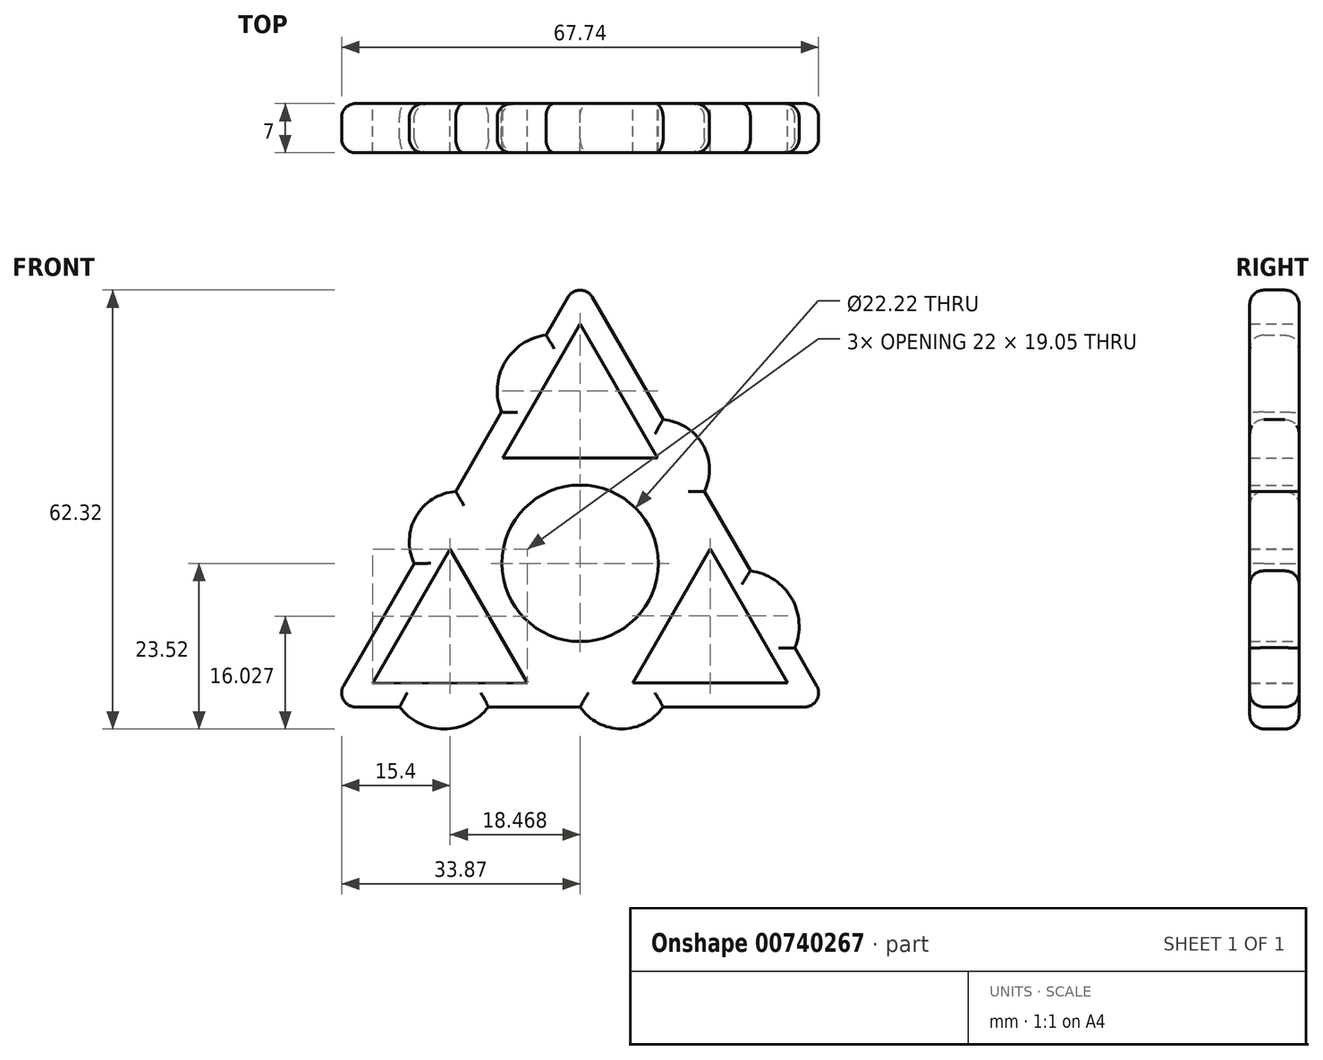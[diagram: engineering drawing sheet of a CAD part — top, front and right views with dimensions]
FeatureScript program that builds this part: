
annotation { "Feature Type Name" : "Feature", "Feature Type Description" : "" }
export const myFeature = defineFeature(function(context is Context, id is Id, definition is map)
    precondition{}
    {
        {
            var Q0;
            Q0=qCreatedBy(makeId("Front.planeOp"),FACE);
            var sketch = newSketch(context, id + "F0", { "sketchPlane" : qUnion([Q0])});
            skCircle(sketch, "E0", {"center": v(0, 0) * mm, "radius": 11.1 * mm});
            skLineSegment(sketch, "E1.0", {"start": v(-35.34, -20.4) * mm, "end": v(0, 40.8) * mm});
            skLineSegment(sketch, "E1.1", {"start": v(0, 40.8) * mm, "end": v(35.34, -20.4) * mm});
            skLineSegment(sketch, "E1.2", {"start": v(35.34, -20.4) * mm, "end": v(-35.33, -20.4) * mm});
            skLineSegment(sketch, "E2.direction1", {"start": v(0, 0.8) * mm, "end": v(25, 0.8) * mm, "construction": true});
            skLineSegment(sketch, "E3.0", {"start": v(-11, 14.98) * mm, "end": v(0, 34.03) * mm});
            skLineSegment(sketch, "E3.1", {"start": v(-11, 14.98) * mm, "end": v(11, 14.98) * mm});
            skLineSegment(sketch, "E3.2", {"start": v(0, 34.03) * mm, "end": v(11, 14.98) * mm});
            skLineSegment(sketch, "E4.0", {"start": v(-18.58, -76.36) * mm, "end": v(-40.67, -38.1) * mm});
            skLineSegment(sketch, "E4.1", {"start": v(-18.58, -76.36) * mm, "end": v(3.5, -38.1) * mm});
            skLineSegment(sketch, "E5.1.0", {"start": v(-7.47, -17.02) * mm, "end": v(-18.47, 2.03) * mm});
            skLineSegment(sketch, "E5.1.1", {"start": v(-7.47, -17.02) * mm, "end": v(-29.47, -17.02) * mm});
            skLineSegment(sketch, "E5.1.2", {"start": v(-29.47, -17.02) * mm, "end": v(-18.47, 2.03) * mm});
            skLineSegment(sketch, "E5.2.0", {"start": v(18.47, 2.04) * mm, "end": v(7.48, -17.01) * mm});
            skLineSegment(sketch, "E5.2.1", {"start": v(18.47, 2.04) * mm, "end": v(29.47, -17.01) * mm});
            skLineSegment(sketch, "E5.2.2", {"start": v(29.47, -17.01) * mm, "end": v(7.48, -17.01) * mm});
            skArc(sketch, "E6", {"start": v(-4.85, 32.4) * mm, "mid": v(-10.71, 28.5) * mm, "end": v(-11.16, 21.48) * mm});
            skArc(sketch, "E7", {"start": v(-17.67, 10.2) * mm, "mid": v(-23.3, 6.66) * mm, "end": v(-23.56, 0) * mm});
            skArc(sketch, "E8.1.0", {"start": v(-25.63, -20.4) * mm, "mid": v(-19.32, -23.52) * mm, "end": v(-13.02, -20.4) * mm});
            skArc(sketch, "E8.1.1", {"start": v(0, -20.4) * mm, "mid": v(5.89, -23.51) * mm, "end": v(11.78, -20.4) * mm});
            skArc(sketch, "E8.2.0", {"start": v(30.48, -12) * mm, "mid": v(30.04, -4.97) * mm, "end": v(24.18, -1.08) * mm});
            skArc(sketch, "E8.2.1", {"start": v(17.67, 10.2) * mm, "mid": v(17.42, 16.86) * mm, "end": v(11.78, 20.4) * mm});
            skSolve(sketch);
        }
        {
            var Q0;
            Q0 = qSketchRegion(id + "F0", true);
            extrude(context, id + "F1", {"entities" : qUnion([Q0]), "depth" : 7 * mm, "offsetDistance" : 25 * mm});
        }
        {
            var Q0;
            Q0=makeQuery(id+"F1.opExtrude","SWEPT_EDGE",EDGE,{"disambiguationData":[OSD([sQuery(id+"F0.wireOp",EDGE,"E1.0"),sQuery(id+"F0.wireOp",EDGE,"E1.1"),sQuery(id+"F0.wireOp",EDGE,"TbrVNuta-voQp-v51U-YrGK-JMvI6IDHDoPP")])]});
            var Q1;
            Q1=makeQuery(id+"F1.opExtrude","SWEPT_EDGE",EDGE,{"disambiguationData":[OSD([sQuery(id+"F0.wireOp",EDGE,"E1.0"),sQuery(id+"F0.wireOp",EDGE,"E1.2")])]});
            var Q2;
            Q2=makeQuery(id+"F1.opExtrude","SWEPT_EDGE",EDGE,{"disambiguationData":[OSD([sQuery(id+"F0.wireOp",EDGE,"E1.1"),sQuery(id+"F0.wireOp",EDGE,"E1.2")])]});
            fillet(context, id + "F2", {"entities" : qUnion([Q0, Q1, Q2]), "radius" : 2 * mm, "tangentPropagation" : true, "allowEdgeOverflow" : false});
        }
        {
            var Q0;
            {var subQ0=sQuery(id+"F0.wireOp",EDGE,"E1.0");Q0=makeQuery(id+"F1.opExtrude","CAP_EDGE",EDGE,{"disambiguationData":[OSD([subQ0]),TDD([makeQuery(id+"F0.imprint","IMPRINT",EDGE,{"disambiguationData":[TD([[makeQuery(id+"F0.imprint","INTERSECT",VERTEX,{"derivedFrom":[subQ0,sQuery(id+"F0.wireOp",EDGE,"E1.2")]}),-1.0]])],"derivedFrom":subQ0})])],"isStart":false});}
            var Q1;
            Q1=makeQuery(id+"F1.opExtrude","CAP_EDGE",EDGE,{"disambiguationData":[OSD([sQuery(id+"F0.wireOp",EDGE,"E7")])],"isStart":false});
            var Q2;
            {var subQ0=sQuery(id+"F0.wireOp",EDGE,"E1.0");Q2=makeQuery(id+"F1.opExtrude","CAP_EDGE",EDGE,{"disambiguationData":[OSD([subQ0]),TDD([makeQuery(id+"F0.imprint","IMPRINT",EDGE,{"disambiguationData":[TD([[makeQuery(id+"F0.imprint","INTERSECT",VERTEX,{"disambiguationData":[OD(1.0)],"derivedFrom":[subQ0,sQuery(id+"F0.wireOp",EDGE,"E6")]}),1.0]])],"derivedFrom":subQ0})])],"isStart":false});}
            var Q3;
            Q3=makeQuery(id+"F1.opExtrude","CAP_EDGE",EDGE,{"disambiguationData":[OSD([sQuery(id+"F0.wireOp",EDGE,"E6")])],"isStart":false});
            var Q4;
            {var subQ0=sQuery(id+"F0.wireOp",EDGE,"E1.0");Q4=makeQuery(id+"F1.opExtrude","CAP_EDGE",EDGE,{"disambiguationData":[OSD([subQ0]),TDD([makeQuery(id+"F0.imprint","IMPRINT",EDGE,{"disambiguationData":[TD([[makeQuery(id+"F0.imprint","INTERSECT",VERTEX,{"derivedFrom":[subQ0,sQuery(id+"F0.wireOp",EDGE,"E1.1")]}),1.0]])],"derivedFrom":subQ0})])],"isStart":false});}
            var Q5;
            {var subQ0=sQuery(id+"F0.wireOp",EDGE,"E1.1");var subQ1=sQuery(id+"F0.wireOp",EDGE,"E1.0");Q5=makeQuery(id+"F2.opFillet","BLEND_EDGE",EDGE,{"blendedFrom":[makeQuery(id+"F1.opExtrude","SWEPT_EDGE",EDGE,{"disambiguationData":[OSD([subQ1,subQ0])]}),makeQuery(id+"F1.opExtrude","CAP_FACE",FACE,{"disambiguationData":[OSD([sQuery(id+"F0.wireOp",EDGE,"E0"),subQ1,subQ0,sQuery(id+"F0.wireOp",EDGE,"E1.2"),sQuery(id+"F0.wireOp",EDGE,"E3.0"),sQuery(id+"F0.wireOp",EDGE,"E3.1"),sQuery(id+"F0.wireOp",EDGE,"E3.2"),sQuery(id+"F0.wireOp",EDGE,"E5.1.0"),sQuery(id+"F0.wireOp",EDGE,"E5.1.1"),sQuery(id+"F0.wireOp",EDGE,"E5.1.2"),sQuery(id+"F0.wireOp",EDGE,"E5.2.0"),sQuery(id+"F0.wireOp",EDGE,"E5.2.1"),sQuery(id+"F0.wireOp",EDGE,"E5.2.2"),sQuery(id+"F0.wireOp",EDGE,"E6"),sQuery(id+"F0.wireOp",EDGE,"E7"),sQuery(id+"F0.wireOp",EDGE,"E8.1.0"),sQuery(id+"F0.wireOp",EDGE,"E8.1.1"),sQuery(id+"F0.wireOp",EDGE,"E8.2.0"),sQuery(id+"F0.wireOp",EDGE,"E8.2.1")])],"isStart":false})],"blendedInto":[makeQuery(id+"F1.opExtrude","CAP_FACE",FACE,{"disambiguationData":[OSD([sQuery(id+"F0.wireOp",EDGE,"E0"),subQ1,subQ0,sQuery(id+"F0.wireOp",EDGE,"E1.2"),sQuery(id+"F0.wireOp",EDGE,"E3.0"),sQuery(id+"F0.wireOp",EDGE,"E3.1"),sQuery(id+"F0.wireOp",EDGE,"E3.2"),sQuery(id+"F0.wireOp",EDGE,"E5.1.0"),sQuery(id+"F0.wireOp",EDGE,"E5.1.1"),sQuery(id+"F0.wireOp",EDGE,"E5.1.2"),sQuery(id+"F0.wireOp",EDGE,"E5.2.0"),sQuery(id+"F0.wireOp",EDGE,"E5.2.1"),sQuery(id+"F0.wireOp",EDGE,"E5.2.2"),sQuery(id+"F0.wireOp",EDGE,"E6"),sQuery(id+"F0.wireOp",EDGE,"E7"),sQuery(id+"F0.wireOp",EDGE,"E8.1.0"),sQuery(id+"F0.wireOp",EDGE,"E8.1.1"),sQuery(id+"F0.wireOp",EDGE,"E8.2.0"),sQuery(id+"F0.wireOp",EDGE,"E8.2.1")])],"isStart":false})]});}
            var Q6;
            {var subQ0=sQuery(id+"F0.wireOp",EDGE,"E1.1");Q6=makeQuery(id+"F1.opExtrude","CAP_EDGE",EDGE,{"disambiguationData":[OSD([subQ0]),TDD([makeQuery(id+"F0.imprint","IMPRINT",EDGE,{"disambiguationData":[TD([[makeQuery(id+"F0.imprint","INTERSECT",VERTEX,{"derivedFrom":[sQuery(id+"F0.wireOp",EDGE,"E1.0"),subQ0]}),-1.0]])],"derivedFrom":subQ0})])],"isStart":false});}
            var Q7;
            Q7=makeQuery(id+"F1.opExtrude","CAP_EDGE",EDGE,{"disambiguationData":[OSD([sQuery(id+"F0.wireOp",EDGE,"E8.2.1")])],"isStart":false});
            var Q8;
            {var subQ0=sQuery(id+"F0.wireOp",EDGE,"E1.1");Q8=makeQuery(id+"F1.opExtrude","CAP_EDGE",EDGE,{"disambiguationData":[OSD([subQ0]),TDD([makeQuery(id+"F0.imprint","IMPRINT",EDGE,{"disambiguationData":[TD([[makeQuery(id+"F0.imprint","INTERSECT",VERTEX,{"disambiguationData":[OD(1.0)],"derivedFrom":[subQ0,sQuery(id+"F0.wireOp",EDGE,"E8.2.0")]}),1.0]])],"derivedFrom":subQ0})])],"isStart":false});}
            var Q9;
            Q9=makeQuery(id+"F1.opExtrude","CAP_EDGE",EDGE,{"disambiguationData":[OSD([sQuery(id+"F0.wireOp",EDGE,"E8.2.0")])],"isStart":false});
            var Q10;
            {var subQ0=sQuery(id+"F0.wireOp",EDGE,"E1.1");Q10=makeQuery(id+"F1.opExtrude","CAP_EDGE",EDGE,{"disambiguationData":[OSD([subQ0]),TDD([makeQuery(id+"F0.imprint","IMPRINT",EDGE,{"disambiguationData":[TD([[makeQuery(id+"F0.imprint","INTERSECT",VERTEX,{"derivedFrom":[subQ0,sQuery(id+"F0.wireOp",EDGE,"E1.2")]}),1.0]])],"derivedFrom":subQ0})])],"isStart":false});}
            var Q11;
            {var subQ0=sQuery(id+"F0.wireOp",EDGE,"E1.2");Q11=makeQuery(id+"F1.opExtrude","CAP_EDGE",EDGE,{"disambiguationData":[OSD([subQ0]),TDD([makeQuery(id+"F0.imprint","IMPRINT",EDGE,{"disambiguationData":[TD([[makeQuery(id+"F0.imprint","INTERSECT",VERTEX,{"derivedFrom":[sQuery(id+"F0.wireOp",EDGE,"E1.1"),subQ0]}),-1.0]])],"derivedFrom":subQ0})])],"isStart":false});}
            var Q12;
            {var subQ0=sQuery(id+"F0.wireOp",EDGE,"E1.2");var subQ1=sQuery(id+"F0.wireOp",EDGE,"E1.1");Q12=makeQuery(id+"F2.opFillet","BLEND_EDGE",EDGE,{"blendedFrom":[makeQuery(id+"F1.opExtrude","SWEPT_EDGE",EDGE,{"disambiguationData":[OSD([subQ1,subQ0])]}),makeQuery(id+"F1.opExtrude","CAP_FACE",FACE,{"disambiguationData":[OSD([sQuery(id+"F0.wireOp",EDGE,"E0"),sQuery(id+"F0.wireOp",EDGE,"E1.0"),subQ1,subQ0,sQuery(id+"F0.wireOp",EDGE,"E3.0"),sQuery(id+"F0.wireOp",EDGE,"E3.1"),sQuery(id+"F0.wireOp",EDGE,"E3.2"),sQuery(id+"F0.wireOp",EDGE,"E5.1.0"),sQuery(id+"F0.wireOp",EDGE,"E5.1.1"),sQuery(id+"F0.wireOp",EDGE,"E5.1.2"),sQuery(id+"F0.wireOp",EDGE,"E5.2.0"),sQuery(id+"F0.wireOp",EDGE,"E5.2.1"),sQuery(id+"F0.wireOp",EDGE,"E5.2.2"),sQuery(id+"F0.wireOp",EDGE,"E6"),sQuery(id+"F0.wireOp",EDGE,"E7"),sQuery(id+"F0.wireOp",EDGE,"E8.1.0"),sQuery(id+"F0.wireOp",EDGE,"E8.1.1"),sQuery(id+"F0.wireOp",EDGE,"E8.2.0"),sQuery(id+"F0.wireOp",EDGE,"E8.2.1")])],"isStart":false})],"blendedInto":[makeQuery(id+"F1.opExtrude","CAP_FACE",FACE,{"disambiguationData":[OSD([sQuery(id+"F0.wireOp",EDGE,"E0"),sQuery(id+"F0.wireOp",EDGE,"E1.0"),subQ1,subQ0,sQuery(id+"F0.wireOp",EDGE,"E3.0"),sQuery(id+"F0.wireOp",EDGE,"E3.1"),sQuery(id+"F0.wireOp",EDGE,"E3.2"),sQuery(id+"F0.wireOp",EDGE,"E5.1.0"),sQuery(id+"F0.wireOp",EDGE,"E5.1.1"),sQuery(id+"F0.wireOp",EDGE,"E5.1.2"),sQuery(id+"F0.wireOp",EDGE,"E5.2.0"),sQuery(id+"F0.wireOp",EDGE,"E5.2.1"),sQuery(id+"F0.wireOp",EDGE,"E5.2.2"),sQuery(id+"F0.wireOp",EDGE,"E6"),sQuery(id+"F0.wireOp",EDGE,"E7"),sQuery(id+"F0.wireOp",EDGE,"E8.1.0"),sQuery(id+"F0.wireOp",EDGE,"E8.1.1"),sQuery(id+"F0.wireOp",EDGE,"E8.2.0"),sQuery(id+"F0.wireOp",EDGE,"E8.2.1")])],"isStart":false})]});}
            var Q13;
            Q13=makeQuery(id+"F1.opExtrude","CAP_EDGE",EDGE,{"disambiguationData":[OSD([sQuery(id+"F0.wireOp",EDGE,"E8.1.1")])],"isStart":false});
            var Q14;
            {var subQ0=sQuery(id+"F0.wireOp",EDGE,"E1.2");Q14=makeQuery(id+"F1.opExtrude","CAP_EDGE",EDGE,{"disambiguationData":[OSD([subQ0]),TDD([makeQuery(id+"F0.imprint","IMPRINT",EDGE,{"disambiguationData":[TD([[makeQuery(id+"F0.imprint","INTERSECT",VERTEX,{"disambiguationData":[OD(1.0)],"derivedFrom":[subQ0,sQuery(id+"F0.wireOp",EDGE,"E8.1.0")]}),1.0]])],"derivedFrom":subQ0})])],"isStart":false});}
            var Q15;
            Q15=makeQuery(id+"F1.opExtrude","CAP_EDGE",EDGE,{"disambiguationData":[OSD([sQuery(id+"F0.wireOp",EDGE,"E8.1.0")])],"isStart":false});
            var Q16;
            {var subQ0=sQuery(id+"F0.wireOp",EDGE,"E1.2");Q16=makeQuery(id+"F1.opExtrude","CAP_EDGE",EDGE,{"disambiguationData":[OSD([subQ0]),TDD([makeQuery(id+"F0.imprint","IMPRINT",EDGE,{"disambiguationData":[TD([[makeQuery(id+"F0.imprint","INTERSECT",VERTEX,{"derivedFrom":[sQuery(id+"F0.wireOp",EDGE,"E1.0"),subQ0]}),1.0]])],"derivedFrom":subQ0})])],"isStart":false});}
            var Q17;
            {var subQ0=sQuery(id+"F0.wireOp",EDGE,"E1.2");var subQ1=sQuery(id+"F0.wireOp",EDGE,"E1.0");Q17=makeQuery(id+"F2.opFillet","BLEND_EDGE",EDGE,{"blendedFrom":[makeQuery(id+"F1.opExtrude","SWEPT_EDGE",EDGE,{"disambiguationData":[OSD([subQ1,subQ0])]}),makeQuery(id+"F1.opExtrude","CAP_FACE",FACE,{"disambiguationData":[OSD([sQuery(id+"F0.wireOp",EDGE,"E0"),subQ1,sQuery(id+"F0.wireOp",EDGE,"E1.1"),subQ0,sQuery(id+"F0.wireOp",EDGE,"E3.0"),sQuery(id+"F0.wireOp",EDGE,"E3.1"),sQuery(id+"F0.wireOp",EDGE,"E3.2"),sQuery(id+"F0.wireOp",EDGE,"E5.1.0"),sQuery(id+"F0.wireOp",EDGE,"E5.1.1"),sQuery(id+"F0.wireOp",EDGE,"E5.1.2"),sQuery(id+"F0.wireOp",EDGE,"E5.2.0"),sQuery(id+"F0.wireOp",EDGE,"E5.2.1"),sQuery(id+"F0.wireOp",EDGE,"E5.2.2"),sQuery(id+"F0.wireOp",EDGE,"E6"),sQuery(id+"F0.wireOp",EDGE,"E7"),sQuery(id+"F0.wireOp",EDGE,"E8.1.0"),sQuery(id+"F0.wireOp",EDGE,"E8.1.1"),sQuery(id+"F0.wireOp",EDGE,"E8.2.0"),sQuery(id+"F0.wireOp",EDGE,"E8.2.1")])],"isStart":false})],"blendedInto":[makeQuery(id+"F1.opExtrude","CAP_FACE",FACE,{"disambiguationData":[OSD([sQuery(id+"F0.wireOp",EDGE,"E0"),subQ1,sQuery(id+"F0.wireOp",EDGE,"E1.1"),subQ0,sQuery(id+"F0.wireOp",EDGE,"E3.0"),sQuery(id+"F0.wireOp",EDGE,"E3.1"),sQuery(id+"F0.wireOp",EDGE,"E3.2"),sQuery(id+"F0.wireOp",EDGE,"E5.1.0"),sQuery(id+"F0.wireOp",EDGE,"E5.1.1"),sQuery(id+"F0.wireOp",EDGE,"E5.1.2"),sQuery(id+"F0.wireOp",EDGE,"E5.2.0"),sQuery(id+"F0.wireOp",EDGE,"E5.2.1"),sQuery(id+"F0.wireOp",EDGE,"E5.2.2"),sQuery(id+"F0.wireOp",EDGE,"E6"),sQuery(id+"F0.wireOp",EDGE,"E7"),sQuery(id+"F0.wireOp",EDGE,"E8.1.0"),sQuery(id+"F0.wireOp",EDGE,"E8.1.1"),sQuery(id+"F0.wireOp",EDGE,"E8.2.0"),sQuery(id+"F0.wireOp",EDGE,"E8.2.1")])],"isStart":false})]});}
            fillet(context, id + "F3", {"entities" : qUnion([Q0, Q1, Q2, Q3, Q4, Q5, Q6, Q7, Q8, Q9, Q10, Q11, Q12, Q13, Q14, Q15, Q16, Q17]), "radius" : 2 * mm, "tangentPropagation" : true, "allowEdgeOverflow" : false});
        }
        {
            var Q0;
            {var subQ0=sQuery(id+"F0.wireOp",EDGE,"E1.1");var subQ1=sQuery(id+"F0.wireOp",EDGE,"E1.0");Q0=makeQuery(id+"F2.opFillet","BLEND_EDGE",EDGE,{"blendedFrom":[makeQuery(id+"F1.opExtrude","SWEPT_EDGE",EDGE,{"disambiguationData":[OSD([subQ1,subQ0])]}),makeQuery(id+"F1.opExtrude","CAP_FACE",FACE,{"disambiguationData":[OSD([sQuery(id+"F0.wireOp",EDGE,"E0"),subQ1,subQ0,sQuery(id+"F0.wireOp",EDGE,"E1.2"),sQuery(id+"F0.wireOp",EDGE,"E3.0"),sQuery(id+"F0.wireOp",EDGE,"E3.1"),sQuery(id+"F0.wireOp",EDGE,"E3.2"),sQuery(id+"F0.wireOp",EDGE,"E5.1.0"),sQuery(id+"F0.wireOp",EDGE,"E5.1.1"),sQuery(id+"F0.wireOp",EDGE,"E5.1.2"),sQuery(id+"F0.wireOp",EDGE,"E5.2.0"),sQuery(id+"F0.wireOp",EDGE,"E5.2.1"),sQuery(id+"F0.wireOp",EDGE,"E5.2.2"),sQuery(id+"F0.wireOp",EDGE,"E6"),sQuery(id+"F0.wireOp",EDGE,"E7"),sQuery(id+"F0.wireOp",EDGE,"E8.1.0"),sQuery(id+"F0.wireOp",EDGE,"E8.1.1"),sQuery(id+"F0.wireOp",EDGE,"E8.2.0"),sQuery(id+"F0.wireOp",EDGE,"E8.2.1")])],"isStart":true})],"blendedInto":[makeQuery(id+"F1.opExtrude","CAP_FACE",FACE,{"disambiguationData":[OSD([sQuery(id+"F0.wireOp",EDGE,"E0"),subQ1,subQ0,sQuery(id+"F0.wireOp",EDGE,"E1.2"),sQuery(id+"F0.wireOp",EDGE,"E3.0"),sQuery(id+"F0.wireOp",EDGE,"E3.1"),sQuery(id+"F0.wireOp",EDGE,"E3.2"),sQuery(id+"F0.wireOp",EDGE,"E5.1.0"),sQuery(id+"F0.wireOp",EDGE,"E5.1.1"),sQuery(id+"F0.wireOp",EDGE,"E5.1.2"),sQuery(id+"F0.wireOp",EDGE,"E5.2.0"),sQuery(id+"F0.wireOp",EDGE,"E5.2.1"),sQuery(id+"F0.wireOp",EDGE,"E5.2.2"),sQuery(id+"F0.wireOp",EDGE,"E6"),sQuery(id+"F0.wireOp",EDGE,"E7"),sQuery(id+"F0.wireOp",EDGE,"E8.1.0"),sQuery(id+"F0.wireOp",EDGE,"E8.1.1"),sQuery(id+"F0.wireOp",EDGE,"E8.2.0"),sQuery(id+"F0.wireOp",EDGE,"E8.2.1")])],"isStart":true})]});}
            var Q1;
            {var subQ0=sQuery(id+"F0.wireOp",EDGE,"E1.1");Q1=makeQuery(id+"F1.opExtrude","CAP_EDGE",EDGE,{"disambiguationData":[OSD([subQ0]),TDD([makeQuery(id+"F0.imprint","IMPRINT",EDGE,{"disambiguationData":[TD([[makeQuery(id+"F0.imprint","INTERSECT",VERTEX,{"derivedFrom":[sQuery(id+"F0.wireOp",EDGE,"E1.0"),subQ0]}),-1.0]])],"derivedFrom":subQ0})])],"isStart":true});}
            var Q2;
            {var subQ0=sQuery(id+"F0.wireOp",EDGE,"E1.0");Q2=makeQuery(id+"F1.opExtrude","CAP_EDGE",EDGE,{"disambiguationData":[OSD([subQ0]),TDD([makeQuery(id+"F0.imprint","IMPRINT",EDGE,{"disambiguationData":[TD([[makeQuery(id+"F0.imprint","INTERSECT",VERTEX,{"derivedFrom":[subQ0,sQuery(id+"F0.wireOp",EDGE,"E1.1")]}),1.0]])],"derivedFrom":subQ0})])],"isStart":true});}
            var Q3;
            Q3=makeQuery(id+"F1.opExtrude","CAP_EDGE",EDGE,{"disambiguationData":[OSD([sQuery(id+"F0.wireOp",EDGE,"E6")])],"isStart":true});
            var Q4;
            {var subQ0=sQuery(id+"F0.wireOp",EDGE,"E1.0");Q4=makeQuery(id+"F1.opExtrude","CAP_EDGE",EDGE,{"disambiguationData":[OSD([subQ0]),TDD([makeQuery(id+"F0.imprint","IMPRINT",EDGE,{"disambiguationData":[TD([[makeQuery(id+"F0.imprint","INTERSECT",VERTEX,{"disambiguationData":[OD(1.0)],"derivedFrom":[subQ0,sQuery(id+"F0.wireOp",EDGE,"E6")]}),1.0]])],"derivedFrom":subQ0})])],"isStart":true});}
            var Q5;
            Q5=makeQuery(id+"F1.opExtrude","CAP_EDGE",EDGE,{"disambiguationData":[OSD([sQuery(id+"F0.wireOp",EDGE,"E7")])],"isStart":true});
            var Q6;
            {var subQ0=sQuery(id+"F0.wireOp",EDGE,"E1.0");Q6=makeQuery(id+"F1.opExtrude","CAP_EDGE",EDGE,{"disambiguationData":[OSD([subQ0]),TDD([makeQuery(id+"F0.imprint","IMPRINT",EDGE,{"disambiguationData":[TD([[makeQuery(id+"F0.imprint","INTERSECT",VERTEX,{"derivedFrom":[subQ0,sQuery(id+"F0.wireOp",EDGE,"E1.2")]}),-1.0]])],"derivedFrom":subQ0})])],"isStart":true});}
            var Q7;
            {var subQ0=sQuery(id+"F0.wireOp",EDGE,"E1.2");var subQ1=sQuery(id+"F0.wireOp",EDGE,"E1.0");Q7=makeQuery(id+"F2.opFillet","BLEND_EDGE",EDGE,{"blendedFrom":[makeQuery(id+"F1.opExtrude","SWEPT_EDGE",EDGE,{"disambiguationData":[OSD([subQ1,subQ0])]}),makeQuery(id+"F1.opExtrude","CAP_FACE",FACE,{"disambiguationData":[OSD([sQuery(id+"F0.wireOp",EDGE,"E0"),subQ1,sQuery(id+"F0.wireOp",EDGE,"E1.1"),subQ0,sQuery(id+"F0.wireOp",EDGE,"E3.0"),sQuery(id+"F0.wireOp",EDGE,"E3.1"),sQuery(id+"F0.wireOp",EDGE,"E3.2"),sQuery(id+"F0.wireOp",EDGE,"E5.1.0"),sQuery(id+"F0.wireOp",EDGE,"E5.1.1"),sQuery(id+"F0.wireOp",EDGE,"E5.1.2"),sQuery(id+"F0.wireOp",EDGE,"E5.2.0"),sQuery(id+"F0.wireOp",EDGE,"E5.2.1"),sQuery(id+"F0.wireOp",EDGE,"E5.2.2"),sQuery(id+"F0.wireOp",EDGE,"E6"),sQuery(id+"F0.wireOp",EDGE,"E7"),sQuery(id+"F0.wireOp",EDGE,"E8.1.0"),sQuery(id+"F0.wireOp",EDGE,"E8.1.1"),sQuery(id+"F0.wireOp",EDGE,"E8.2.0"),sQuery(id+"F0.wireOp",EDGE,"E8.2.1")])],"isStart":true})],"blendedInto":[makeQuery(id+"F1.opExtrude","CAP_FACE",FACE,{"disambiguationData":[OSD([sQuery(id+"F0.wireOp",EDGE,"E0"),subQ1,sQuery(id+"F0.wireOp",EDGE,"E1.1"),subQ0,sQuery(id+"F0.wireOp",EDGE,"E3.0"),sQuery(id+"F0.wireOp",EDGE,"E3.1"),sQuery(id+"F0.wireOp",EDGE,"E3.2"),sQuery(id+"F0.wireOp",EDGE,"E5.1.0"),sQuery(id+"F0.wireOp",EDGE,"E5.1.1"),sQuery(id+"F0.wireOp",EDGE,"E5.1.2"),sQuery(id+"F0.wireOp",EDGE,"E5.2.0"),sQuery(id+"F0.wireOp",EDGE,"E5.2.1"),sQuery(id+"F0.wireOp",EDGE,"E5.2.2"),sQuery(id+"F0.wireOp",EDGE,"E6"),sQuery(id+"F0.wireOp",EDGE,"E7"),sQuery(id+"F0.wireOp",EDGE,"E8.1.0"),sQuery(id+"F0.wireOp",EDGE,"E8.1.1"),sQuery(id+"F0.wireOp",EDGE,"E8.2.0"),sQuery(id+"F0.wireOp",EDGE,"E8.2.1")])],"isStart":true})]});}
            var Q8;
            {var subQ0=sQuery(id+"F0.wireOp",EDGE,"E1.2");Q8=makeQuery(id+"F1.opExtrude","CAP_EDGE",EDGE,{"disambiguationData":[OSD([subQ0]),TDD([makeQuery(id+"F0.imprint","IMPRINT",EDGE,{"disambiguationData":[TD([[makeQuery(id+"F0.imprint","INTERSECT",VERTEX,{"derivedFrom":[sQuery(id+"F0.wireOp",EDGE,"E1.0"),subQ0]}),1.0]])],"derivedFrom":subQ0})])],"isStart":true});}
            var Q9;
            Q9=makeQuery(id+"F1.opExtrude","CAP_EDGE",EDGE,{"disambiguationData":[OSD([sQuery(id+"F0.wireOp",EDGE,"E8.1.0")])],"isStart":true});
            var Q10;
            {var subQ0=sQuery(id+"F0.wireOp",EDGE,"E1.2");Q10=makeQuery(id+"F1.opExtrude","CAP_EDGE",EDGE,{"disambiguationData":[OSD([subQ0]),TDD([makeQuery(id+"F0.imprint","IMPRINT",EDGE,{"disambiguationData":[TD([[makeQuery(id+"F0.imprint","INTERSECT",VERTEX,{"disambiguationData":[OD(1.0)],"derivedFrom":[subQ0,sQuery(id+"F0.wireOp",EDGE,"E8.1.0")]}),1.0]])],"derivedFrom":subQ0})])],"isStart":true});}
            var Q11;
            Q11=makeQuery(id+"F1.opExtrude","CAP_EDGE",EDGE,{"disambiguationData":[OSD([sQuery(id+"F0.wireOp",EDGE,"E8.1.1")])],"isStart":true});
            var Q12;
            {var subQ0=sQuery(id+"F0.wireOp",EDGE,"E1.2");Q12=makeQuery(id+"F1.opExtrude","CAP_EDGE",EDGE,{"disambiguationData":[OSD([subQ0]),TDD([makeQuery(id+"F0.imprint","IMPRINT",EDGE,{"disambiguationData":[TD([[makeQuery(id+"F0.imprint","INTERSECT",VERTEX,{"derivedFrom":[sQuery(id+"F0.wireOp",EDGE,"E1.1"),subQ0]}),-1.0]])],"derivedFrom":subQ0})])],"isStart":true});}
            var Q13;
            {var subQ0=sQuery(id+"F0.wireOp",EDGE,"E1.1");Q13=makeQuery(id+"F1.opExtrude","CAP_EDGE",EDGE,{"disambiguationData":[OSD([subQ0]),TDD([makeQuery(id+"F0.imprint","IMPRINT",EDGE,{"disambiguationData":[TD([[makeQuery(id+"F0.imprint","INTERSECT",VERTEX,{"derivedFrom":[subQ0,sQuery(id+"F0.wireOp",EDGE,"E1.2")]}),1.0]])],"derivedFrom":subQ0})])],"isStart":true});}
            var Q14;
            {var subQ0=sQuery(id+"F0.wireOp",EDGE,"E1.2");var subQ1=sQuery(id+"F0.wireOp",EDGE,"E1.1");Q14=makeQuery(id+"F2.opFillet","BLEND_EDGE",EDGE,{"blendedFrom":[makeQuery(id+"F1.opExtrude","SWEPT_EDGE",EDGE,{"disambiguationData":[OSD([subQ1,subQ0])]}),makeQuery(id+"F1.opExtrude","CAP_FACE",FACE,{"disambiguationData":[OSD([sQuery(id+"F0.wireOp",EDGE,"E0"),sQuery(id+"F0.wireOp",EDGE,"E1.0"),subQ1,subQ0,sQuery(id+"F0.wireOp",EDGE,"E3.0"),sQuery(id+"F0.wireOp",EDGE,"E3.1"),sQuery(id+"F0.wireOp",EDGE,"E3.2"),sQuery(id+"F0.wireOp",EDGE,"E5.1.0"),sQuery(id+"F0.wireOp",EDGE,"E5.1.1"),sQuery(id+"F0.wireOp",EDGE,"E5.1.2"),sQuery(id+"F0.wireOp",EDGE,"E5.2.0"),sQuery(id+"F0.wireOp",EDGE,"E5.2.1"),sQuery(id+"F0.wireOp",EDGE,"E5.2.2"),sQuery(id+"F0.wireOp",EDGE,"E6"),sQuery(id+"F0.wireOp",EDGE,"E7"),sQuery(id+"F0.wireOp",EDGE,"E8.1.0"),sQuery(id+"F0.wireOp",EDGE,"E8.1.1"),sQuery(id+"F0.wireOp",EDGE,"E8.2.0"),sQuery(id+"F0.wireOp",EDGE,"E8.2.1")])],"isStart":true})],"blendedInto":[makeQuery(id+"F1.opExtrude","CAP_FACE",FACE,{"disambiguationData":[OSD([sQuery(id+"F0.wireOp",EDGE,"E0"),sQuery(id+"F0.wireOp",EDGE,"E1.0"),subQ1,subQ0,sQuery(id+"F0.wireOp",EDGE,"E3.0"),sQuery(id+"F0.wireOp",EDGE,"E3.1"),sQuery(id+"F0.wireOp",EDGE,"E3.2"),sQuery(id+"F0.wireOp",EDGE,"E5.1.0"),sQuery(id+"F0.wireOp",EDGE,"E5.1.1"),sQuery(id+"F0.wireOp",EDGE,"E5.1.2"),sQuery(id+"F0.wireOp",EDGE,"E5.2.0"),sQuery(id+"F0.wireOp",EDGE,"E5.2.1"),sQuery(id+"F0.wireOp",EDGE,"E5.2.2"),sQuery(id+"F0.wireOp",EDGE,"E6"),sQuery(id+"F0.wireOp",EDGE,"E7"),sQuery(id+"F0.wireOp",EDGE,"E8.1.0"),sQuery(id+"F0.wireOp",EDGE,"E8.1.1"),sQuery(id+"F0.wireOp",EDGE,"E8.2.0"),sQuery(id+"F0.wireOp",EDGE,"E8.2.1")])],"isStart":true})]});}
            var Q15;
            Q15=makeQuery(id+"F1.opExtrude","CAP_EDGE",EDGE,{"disambiguationData":[OSD([sQuery(id+"F0.wireOp",EDGE,"E8.2.0")])],"isStart":true});
            var Q16;
            {var subQ0=sQuery(id+"F0.wireOp",EDGE,"E1.1");Q16=makeQuery(id+"F1.opExtrude","CAP_EDGE",EDGE,{"disambiguationData":[OSD([subQ0]),TDD([makeQuery(id+"F0.imprint","IMPRINT",EDGE,{"disambiguationData":[TD([[makeQuery(id+"F0.imprint","INTERSECT",VERTEX,{"disambiguationData":[OD(1.0)],"derivedFrom":[subQ0,sQuery(id+"F0.wireOp",EDGE,"E8.2.0")]}),1.0]])],"derivedFrom":subQ0})])],"isStart":true});}
            var Q17;
            Q17=makeQuery(id+"F1.opExtrude","CAP_EDGE",EDGE,{"disambiguationData":[OSD([sQuery(id+"F0.wireOp",EDGE,"E8.2.1")])],"isStart":true});
            fillet(context, id + "F4", {"entities" : qUnion([Q0, Q1, Q2, Q3, Q4, Q5, Q6, Q7, Q8, Q9, Q10, Q11, Q12, Q13, Q14, Q15, Q16, Q17]), "radius" : 2 * mm, "tangentPropagation" : true, "allowEdgeOverflow" : false});
        }
    });
